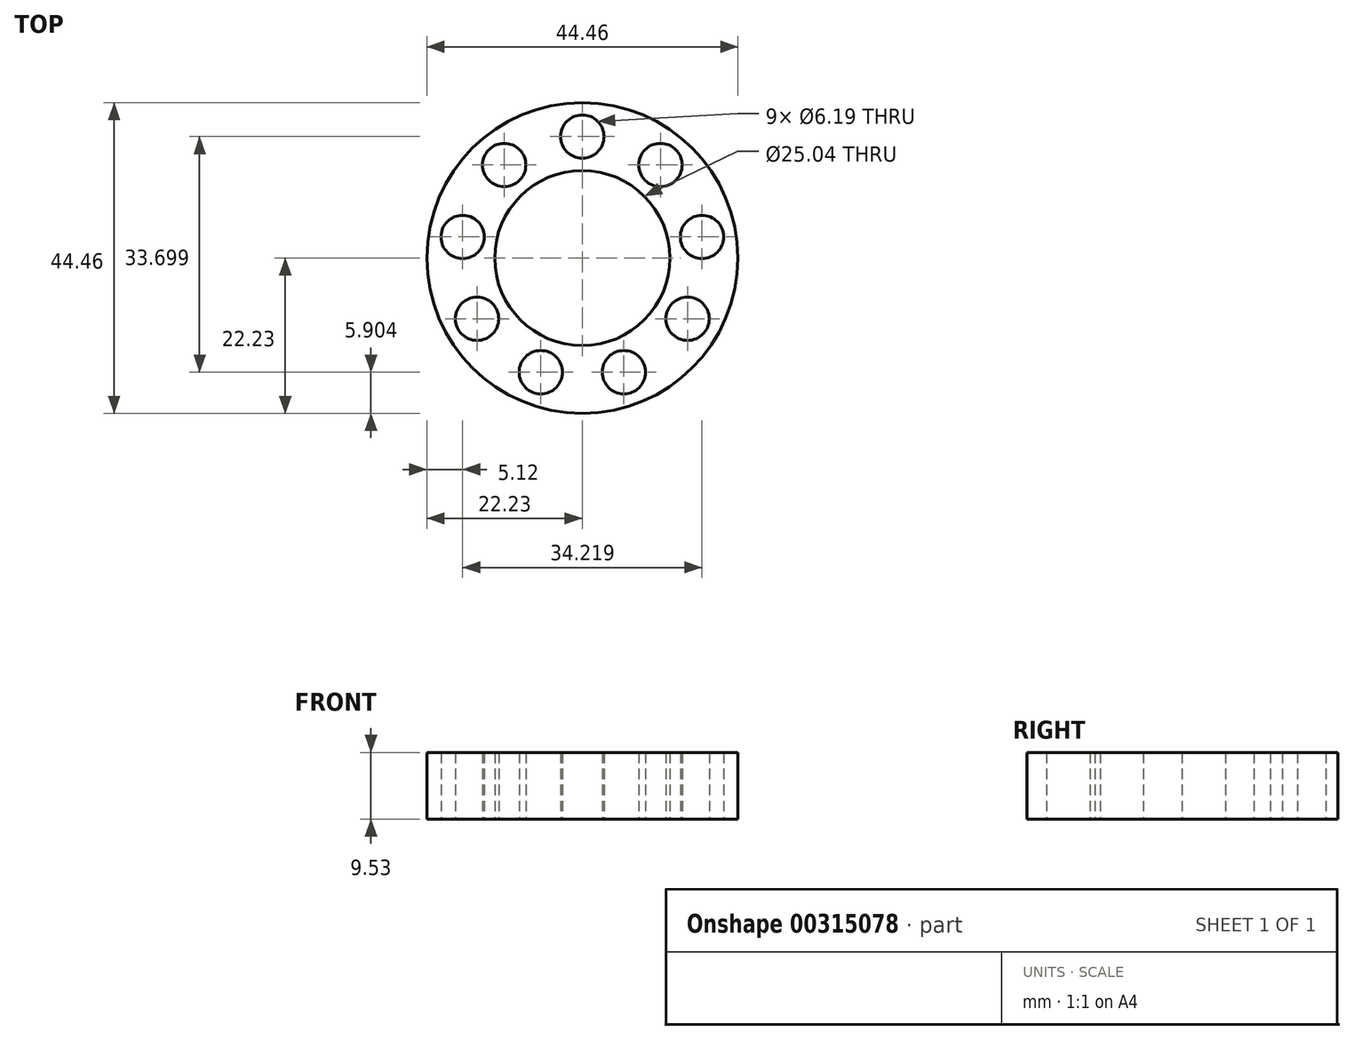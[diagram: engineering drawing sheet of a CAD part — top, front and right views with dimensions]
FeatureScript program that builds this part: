
annotation { "Feature Type Name" : "Feature", "Feature Type Description" : "" }
export const myFeature = defineFeature(function(context is Context, id is Id, definition is map)
    precondition{}
    {
        {
            var Q0;
            Q0=qCreatedBy(makeId("Top.planeOp"),FACE);
            var sketch = newSketch(context, id + "F0", { "sketchPlane" : qUnion([Q0])});
            skCircle(sketch, "E0", {"center": v(0, 0) * mm, "radius": 22.23 * mm});
            skCircle(sketch, "E1", {"center": v(0, 0) * mm, "radius": 12.52 * mm});
            skLineSegment(sketch, "E2", {"start": v(0, 22.23) * mm, "end": v(0, 12.52) * mm, "construction": true});
            skCircle(sketch, "E3", {"center": v(0, 17.37) * mm, "radius": 3.1 * mm});
            skCircle(sketch, "E4.1.0", {"center": v(-11.17, 13.3) * mm, "radius": 3.1 * mm});
            skCircle(sketch, "E4.2.0", {"center": v(-17.1, 3.02) * mm, "radius": 3.1 * mm});
            skCircle(sketch, "E4.3.0", {"center": v(-15.05, -8.69) * mm, "radius": 3.1 * mm});
            skCircle(sketch, "E4.4.0", {"center": v(-5.94, -16.33) * mm, "radius": 3.1 * mm});
            skCircle(sketch, "E4.5.0", {"center": v(5.94, -16.33) * mm, "radius": 3.1 * mm});
            skCircle(sketch, "E4.6.0", {"center": v(15.05, -8.69) * mm, "radius": 3.1 * mm});
            skCircle(sketch, "E4.7.0", {"center": v(17.1, 3.02) * mm, "radius": 3.1 * mm});
            skCircle(sketch, "E4.8.0", {"center": v(11.17, 13.3) * mm, "radius": 3.1 * mm});
            skSolve(sketch);
        }
        {
            var Q0;
            Q0=makeQuery(id+"F0.imprint","IMPRINT",FACE,{"disambiguationData":[TD([[makeQuery(id+"F0.imprint","IMPRINT",EDGE,{"derivedFrom":sQuery(id+"F0.wireOp",EDGE,"E0")}),1.0]])]});
            extrude(context, id + "F1", {"entities" : qUnion([Q0]), "depth" : 9.52 * mm});
        }
    });
